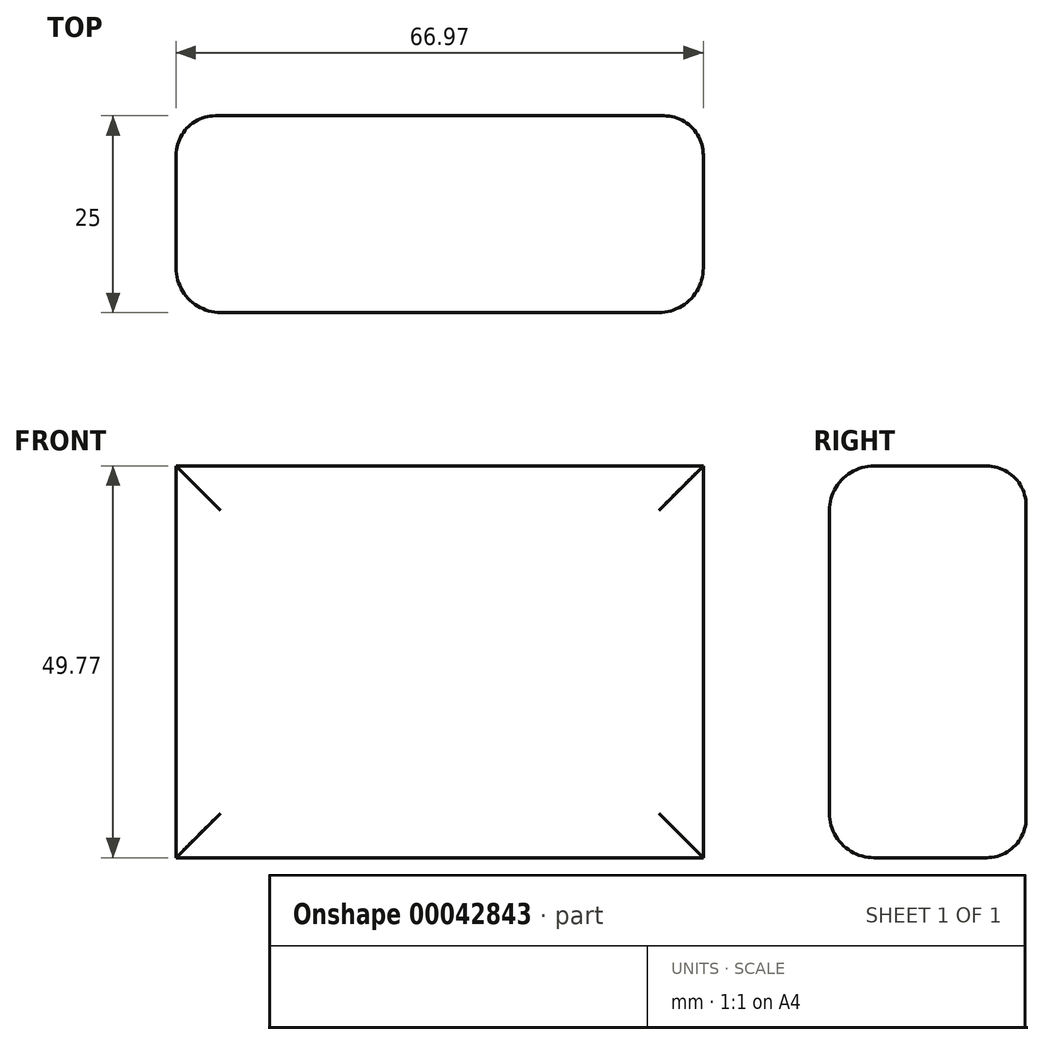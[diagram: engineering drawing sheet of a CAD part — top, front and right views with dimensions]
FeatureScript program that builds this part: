
annotation { "Feature Type Name" : "Feature", "Feature Type Description" : "" }
export const myFeature = defineFeature(function(context is Context, id is Id, definition is map)
    precondition{}
    {
        {
            var Q0;
            Q0=qCreatedBy(makeId("Front.planeOp"),FACE);
            var sketch = newSketch(context, id + "F0", { "sketchPlane" : qUnion([Q0])});
            skLineSegment(sketch, "E0.bottom", {"start": v(-31.63, 25.8) * mm, "end": v(35.34, 25.8) * mm});
            skLineSegment(sketch, "E0.top", {"start": v(-31.63, -23.96) * mm, "end": v(35.34, -23.96) * mm});
            skLineSegment(sketch, "E0.left", {"start": v(-31.63, 25.8) * mm, "end": v(-31.63, -23.96) * mm});
            skLineSegment(sketch, "E0.right", {"start": v(35.34, 25.8) * mm, "end": v(35.34, -23.96) * mm});
            skSolve(sketch);
        }
        {
            var Q0;
            Q0=makeQuery(id+"F0.imprint","IMPRINT",FACE,{"disambiguationData":[TD([[makeQuery(id+"F0.imprint","IMPRINT",EDGE,{"derivedFrom":sQuery(id+"F0.wireOp",EDGE,"E0.bottom")}),-1.0]])]});
            extrude(context, id + "F1", {"entities" : qUnion([Q0]), "depth" : 25 * mm});
        }
        {
            var Q0;
            Q0=makeQuery(id+"F1.opExtrude","CAP_FACE",FACE,{"disambiguationData":[OSD([sQuery(id+"F0.wireOp",EDGE,"E0.bottom"),sQuery(id+"F0.wireOp",EDGE,"E0.top"),sQuery(id+"F0.wireOp",EDGE,"E0.left"),sQuery(id+"F0.wireOp",EDGE,"E0.right")])],"isStart":false});
            fillet(context, id + "F2", {"entities" : qUnion([Q0]), "radius" : 5.66 * mm, "tangentPropagation" : true, "allowEdgeOverflow" : false});
        }
        {
            var Q0;
            Q0=makeQuery(id+"F1.opExtrude","CAP_FACE",FACE,{"disambiguationData":[OSD([sQuery(id+"F0.wireOp",EDGE,"E0.bottom"),sQuery(id+"F0.wireOp",EDGE,"E0.top"),sQuery(id+"F0.wireOp",EDGE,"E0.left"),sQuery(id+"F0.wireOp",EDGE,"E0.right")])],"isStart":true});
            fillet(context, id + "F3", {"entities" : qUnion([Q0]), "radius" : 5 * mm, "tangentPropagation" : true, "allowEdgeOverflow" : false});
        }
    });
